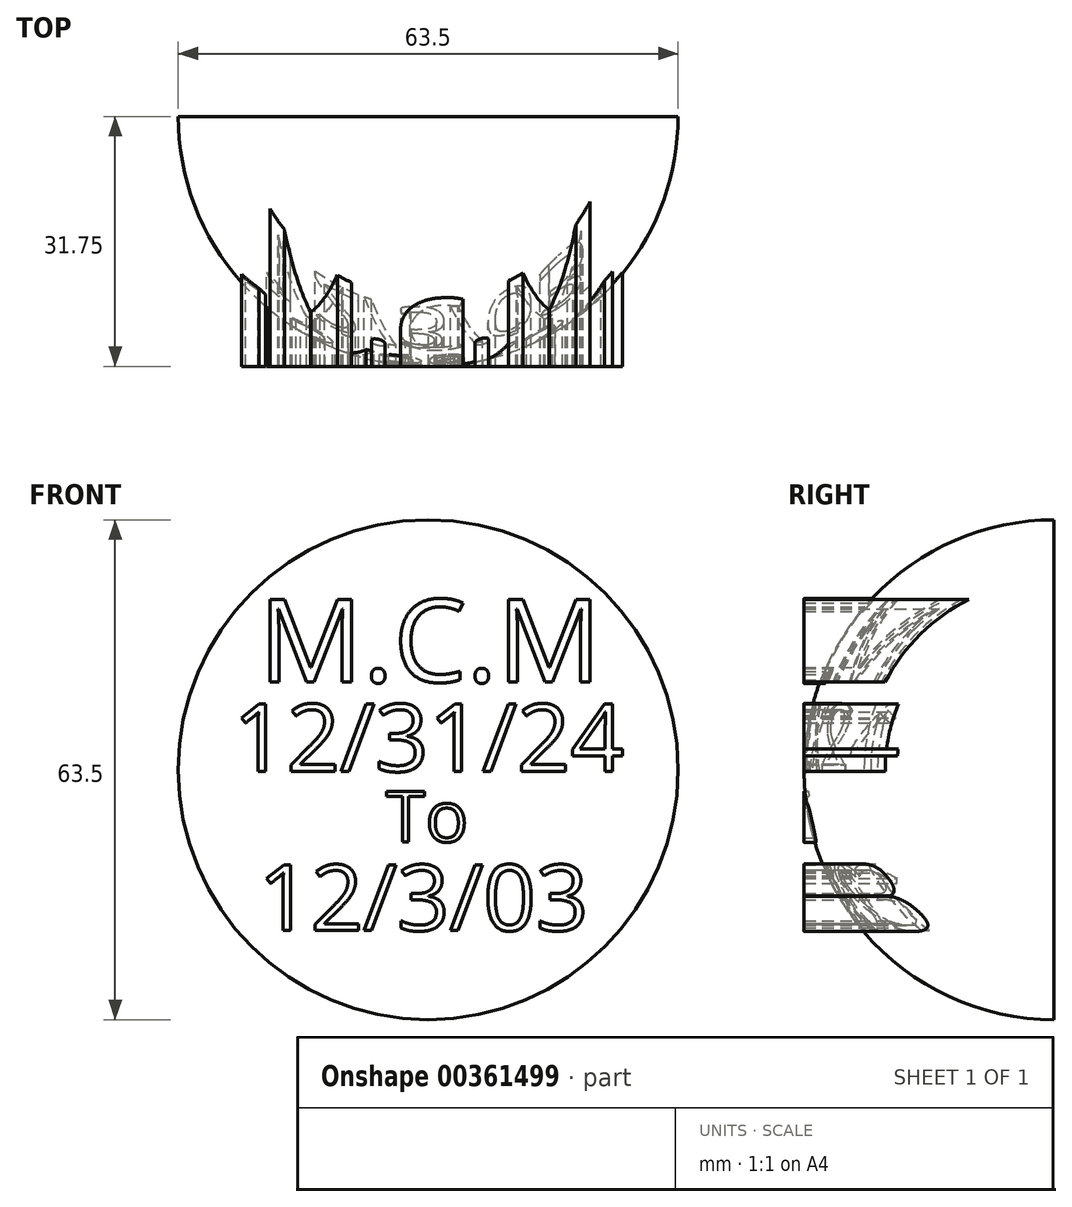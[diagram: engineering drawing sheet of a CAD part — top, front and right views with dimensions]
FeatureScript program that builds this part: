
annotation { "Feature Type Name" : "Feature", "Feature Type Description" : "" }
export const myFeature = defineFeature(function(context is Context, id is Id, definition is map)
    precondition{}
    {
        {
            var Q0;
            Q0=qCreatedBy(makeId("Front.planeOp"),FACE);
            var sketch = newSketch(context, id + "F0", { "sketchPlane" : qUnion([Q0])});
            skArc(sketch, "E0", {"start": v(0, -31.75) * mm, "mid": v(31.75, 0) * mm, "end": v(0, 31.75) * mm});
            skLineSegment(sketch, "E1", {"start": v(0, 31.75) * mm, "end": v(0, -31.75) * mm});
            skSolve(sketch);
        }
        {
            var Q0;
            Q0=makeQuery(id+"F0.imprint","IMPRINT",FACE,{"disambiguationData":[TD([[makeQuery(id+"F0.imprint","IMPRINT",EDGE,{"derivedFrom":sQuery(id+"F0.wireOp",EDGE,"E0")}),1.0]])]});
            var Q1;
            Q1=sQuery(id+"F0.wireOp",EDGE,"E1");
            revolve(context, id + "F1", {"entities" : qUnion([Q0]), "axis" : qUnion([Q1]), "revolveType" : RevolveType.ONE_DIRECTION, "angle" : 180 * degree});
        }
        {
            var Q0;
            Q0=qCreatedBy(makeId("Front.planeOp"),FACE);
            var sketch = newSketch(context, id + "F2", { "sketchPlane" : qUnion([Q0])});
            skText(sketch, "E2", { "text": "M.C.M\n", "fontName": "OpenSans-Regular.ttf"});
            const initialGuessF2  = {"E2": [-0.02153, 0.01116, 1, 0, 0.01056]};
            skSetInitialGuess(sketch, initialGuessF2);
            skSolve(sketch);
        }
        {
            var Q0;
            Q0 = qSketchRegion(id + "F2", true);
            extrude(context, id + "F3", {"entities" : qUnion([Q0]), "operationType" : NewBodyOperationType.ADD, "depth" : 31.75 * mm});
        }
        {
            var Q0;
            Q0=qCreatedBy(makeId("Front.planeOp"),FACE);
            var sketch = newSketch(context, id + "F4", { "sketchPlane" : qUnion([Q0])});
            skText(sketch, "E3", { "text": "12/31/24", "fontName": "OpenSans-Regular.ttf"});
            skText(sketch, "E4", { "text": "To", "fontName": "OpenSans-Regular.ttf"});
            skText(sketch, "E5", { "text": "12/3/03", "fontName": "OpenSans-Regular.ttf"});
            const initialGuessF4  = {"E3": [-0.02482, -0.0002, 1, 0, 0.0086], "E4": [-0.00535, -0.00917, 1, 0, 0.0065], "E5": [-0.02158, -0.02043, 1, 0, 0.0084]};
            skSetInitialGuess(sketch, initialGuessF4);
            skSolve(sketch);
        }
        {
            var Q0;
            Q0 = qSketchRegion(id + "F4", true);
            extrude(context, id + "F5", {"entities" : qUnion([Q0]), "operationType" : NewBodyOperationType.ADD, "depth" : 31.75 * mm});
        }
    });
